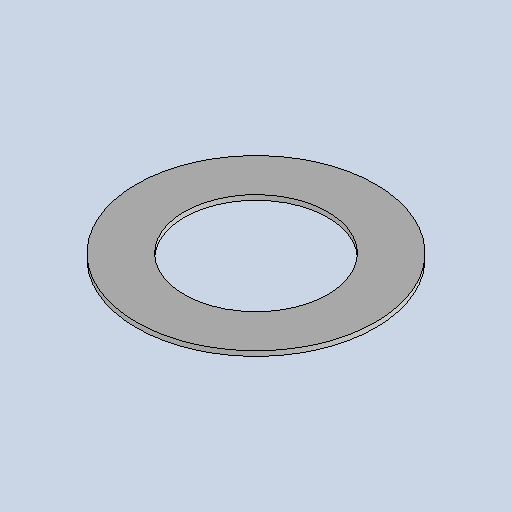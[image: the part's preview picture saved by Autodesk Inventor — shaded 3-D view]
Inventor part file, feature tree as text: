
AUTODESK INVENTOR PART (.ipt)
format: ipt  version: 2025 (Build 290162010, 162A)  size: 92,672 bytes
history: native  units: mm
features: other x2, sheet_metal_op x1, sketch x1
ambient origin geometry x8: Origin, YZ Plane, XZ Plane, XY Plane, X Axis, Y Axis, Z Axis, Center Point
bodies: Solid1 (feature_tree)
feature tree (4):
  other  "MSC 0392 flange"
  sheet_metal_op  "Face1"
  sketch  "Sketch1"  dims[d0=89.9mm d1=149.9mm d2=3.048mm]
  other  "Plate1"
